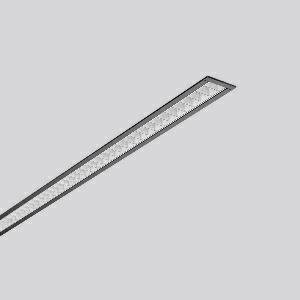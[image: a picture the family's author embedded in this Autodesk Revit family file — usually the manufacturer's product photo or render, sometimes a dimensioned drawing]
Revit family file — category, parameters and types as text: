
# Revit family: less_is_more_27_312177_003_76_ad7b
name_source: partatom
category: Lighting Fixtures
units: mm (PartAtom-declared; Revit-internal decimal feet)

## family parameters
Cut with Voids When Loaded = No
Host = Face
Light Source = No
Part Type = Normal
Room Calculation Point = No
Round Connector Dimension = Use Diameter
Shared = No

## types (1)
- LESS IS MORE 27 (1 x LED Modul 830, 2350 lm, 3000)
    Apparent Load = 29 VA
    CIE Flux Codes = 90 99 100 100 100
    Color Rendering = 80
    Color Temperature = 3000
    Default Elevation = 1800 mm
    Description = Series: LESS IS MORE 27
Recessed ceiling and wall luminaire with slim design. Housing: extruded aluminium profile, powder-coated. End cap aluminium powder-coated. High polish aluminium micro grid. Perfect for office areas (RUG < 19) and environments with computer screens in accordance with EN 12464-1. Suitable for Recessed ceiling mounting, wall (recessed). External driver with connecting cable. 
Colour: deep black, matt (RAL 9005)
Length: 1014 mm
Width: 38 mm
Height: 2 mm
Cut-out length: 1006 mm
Cut-out width: 30 mm
Recess height: 45-60 mm
Luminaire: recess height: 37 mm
Lamp: LED
Socket: without socket
Colour temperature: 3000K
Colour rendering index (CRI): 82
System power: 29 W
Rated luminous flux: 2350 lm
Luminous efficiency: 81 lm/W
Control gear: Voltage converter, DALI dim.
Protection class: II
Type of protection: IP 20
    Height = 0 mm  [stored 0 ft]
    Lamp = 1 x LED Modul 830
    Lamp Light Flux = 2350 lm
    Lamp count = 1
    Length = 1014 mm
    Lifetime = 50000 h
    Luminous efficacy = 81 lm/W
    Manufacturer = RZB
    ModVariant = No
    Model = 312177.003.76
    Mounting Place = Ceiling, Wall
    Mounting Type = Recessed
    Number of Poles = 1
    OnlyDefault = Yes
    Power Factor = 1
    Product Name = LESS IS MORE 27
    Product group = Recessed LED linear luminaires
    ProductGroupID = 407
    Protection Class = Protection class II
    Protection Degree = IP 20
    RLX_Detail_Level = 1
    RLX_Emergency_Light_Flux = 0 lm
    RLX_Emergency_Type = 0
    RLX_Emergency_Type_DB = No
    RlxData = <blob elided: 29885 chars, md5=c6eb2b92>
    Socket = socket
    Standby Power = 0 W
    System Light Flux = 2350 lm
    System Power = 29 W
    Type Comments = Product without accessories
    Type Image = 312177.003.jpg
    URL = http://relux.com
    VarID = ---
    Voltage = 230 V
    Voltage Range = 220-240 V
    Weight = 0.00 kg
    Width = 38 mm

note: [stored X ft] marks values corroborated as IEEE doubles in the binary element streams (Revit-internal decimal feet)

## geometry (parser evidence)
native form markers: Blend x4, Sweep x9
no freeform markers — native parametric forms only
